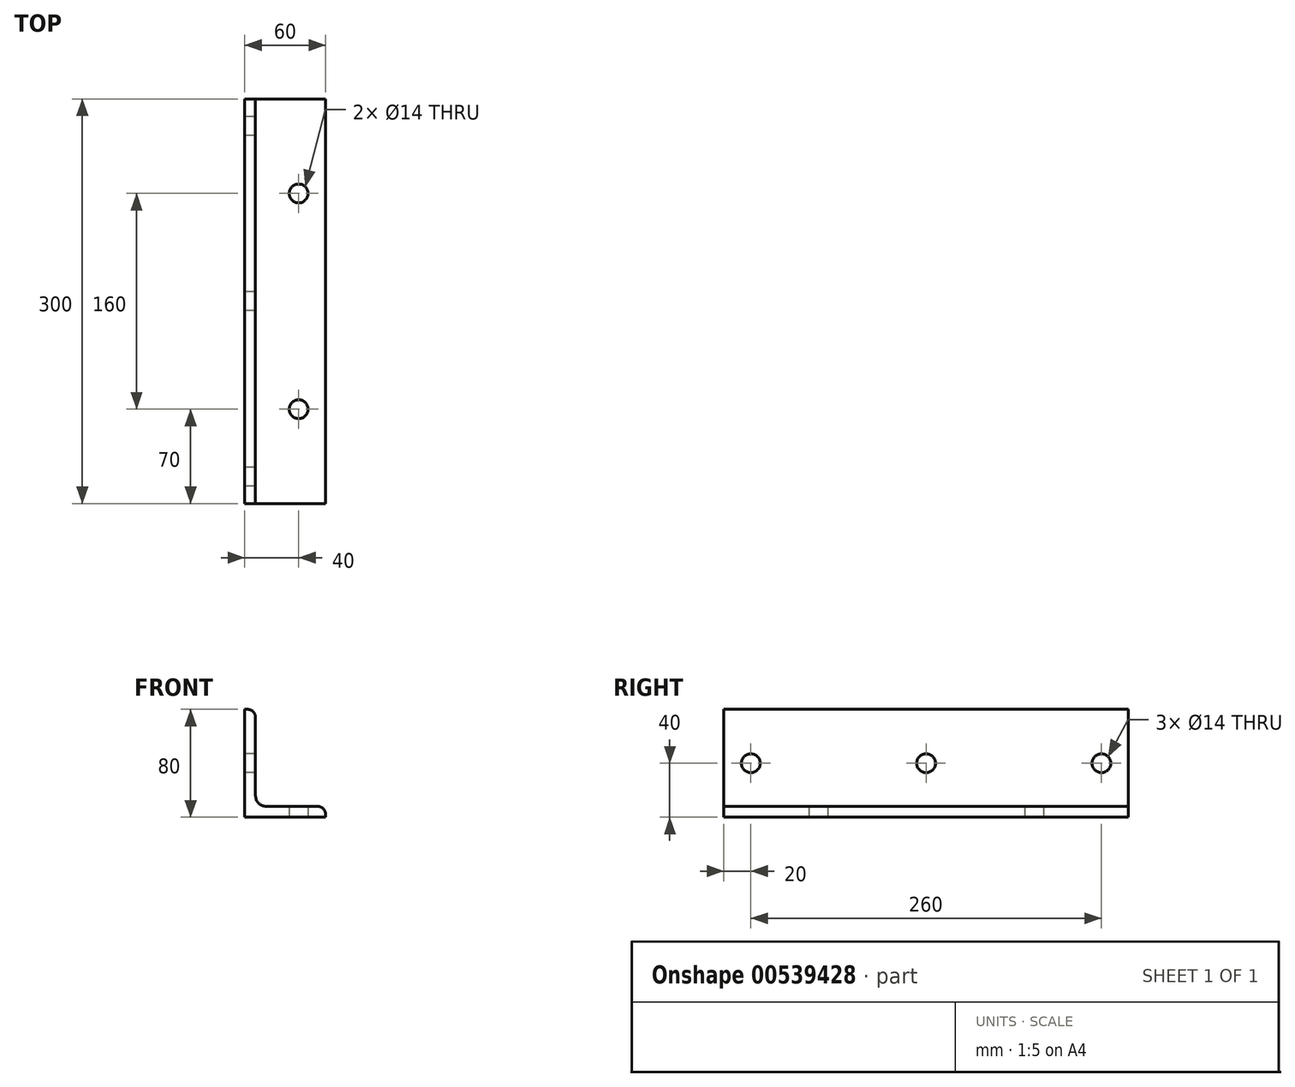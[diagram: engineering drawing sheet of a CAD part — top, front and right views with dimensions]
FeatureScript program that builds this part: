
annotation { "Feature Type Name" : "Feature", "Feature Type Description" : "" }
export const myFeature = defineFeature(function(context is Context, id is Id, definition is map)
    precondition{}
    {
        {
            var Q0;
            Q0=qCreatedBy(makeId("Front.planeOp"),FACE);
            var sketch = newSketch(context, id + "F0", { "sketchPlane" : qUnion([Q0])});
            skLineSegment(sketch, "E0", {"start": v(0, 0) * mm, "end": v(-60, 0) * mm});
            skLineSegment(sketch, "E1", {"start": v(-60, 0) * mm, "end": v(-60, 80) * mm});
            skLineSegment(sketch, "E2", {"start": v(-60, 80) * mm, "end": v(-58, 80) * mm});
            skLineSegment(sketch, "E3", {"start": v(-52, 74) * mm, "end": v(-52, 16) * mm});
            skLineSegment(sketch, "E4", {"start": v(-44, 8) * mm, "end": v(-6, 8) * mm});
            skLineSegment(sketch, "E5", {"start": v(0, 2) * mm, "end": v(0, 0) * mm});
            skPoint(sketch, "E6.visualSharp", {"position": v(-52, 8) * mm});
            skArc(sketch, "E6.filletArc", {"start": v(-52, 16) * mm, "mid": v(-49.66, 10.34) * mm, "end": v(-44, 8) * mm});
            skPoint(sketch, "E7.visualSharp", {"position": v(0, 8) * mm});
            skArc(sketch, "E7.filletArc", {"start": v(0, 2) * mm, "mid": v(-1.76, 6.24) * mm, "end": v(-6, 8) * mm});
            skPoint(sketch, "E8.visualSharp", {"position": v(-52, 80) * mm});
            skArc(sketch, "E8.filletArc", {"start": v(-52, 74) * mm, "mid": v(-53.76, 78.24) * mm, "end": v(-58, 80) * mm});
            skSolve(sketch);
        }
        {
            var Q0;
            Q0=makeQuery(id+"F0.imprint","IMPRINT",FACE,{"disambiguationData":[TD([[makeQuery(id+"F0.imprint","IMPRINT",EDGE,{"derivedFrom":sQuery(id+"F0.wireOp",EDGE,"E0")}),-1.0]])]});
            extrude(context, id + "F1", {"entities" : qUnion([Q0]), "depth" : 300 * mm, "offsetDistance" : 25 * mm});
        }
        {
            var Q0;
            Q0=makeQuery(id+"F1.opExtrude","SWEPT_FACE",FACE,{"disambiguationData":[OSD([sQuery(id+"F0.wireOp",EDGE,"E1")])]});
            var sketch = newSketch(context, id + "F2", { "sketchPlane" : qUnion([Q0])});
            skCircle(sketch, "E9", {"center": v(20, 40) * mm, "radius": 7 * mm});
            skCircle(sketch, "E10", {"center": v(150, 40) * mm, "radius": 7 * mm});
            skCircle(sketch, "E11", {"center": v(280, 40) * mm, "radius": 7 * mm});
            skLineSegment(sketch, "E12", {"start": v(-43.82, 40) * mm, "end": v(392.42, 40) * mm, "construction": true});
            skLineSegment(sketch, "E13", {"start": v(150, 92.91) * mm, "end": v(150, -38.08) * mm, "construction": true});
            skPoint(sketch, "E13.startSnap0", {"position": v(150, 80) * mm});
            skSolve(sketch);
        }
        {
            var Q0;
            Q0 = qSketchRegion(id + "F2", true);
            extrude(context, id + "F3", {"entities" : qUnion([Q0]), "operationType" : NewBodyOperationType.REMOVE, "oppositeDirection" : true, "depth" : 25 * mm, "offsetDistance" : 25 * mm});
        }
        {
            var Q0;
            Q0=makeQuery(id+"F1.opExtrude","SWEPT_FACE",FACE,{"disambiguationData":[OSD([sQuery(id+"F0.wireOp",EDGE,"E0")])]});
            var sketch = newSketch(context, id + "F4", { "sketchPlane" : qUnion([Q0])});
            skCircle(sketch, "E14", {"center": v(-20, 70) * mm, "radius": 7 * mm});
            skCircle(sketch, "E15", {"center": v(-20, 230) * mm, "radius": 7 * mm});
            skLineSegment(sketch, "E16", {"start": v(-60, 150) * mm, "end": v(0, 150) * mm, "construction": true});
            skSolve(sketch);
        }
        {
            var Q0;
            Q0 = qSketchRegion(id + "F4", true);
            extrude(context, id + "F5", {"entities" : qUnion([Q0]), "operationType" : NewBodyOperationType.REMOVE, "oppositeDirection" : true, "depth" : 25 * mm, "offsetDistance" : 25 * mm});
        }
    });
